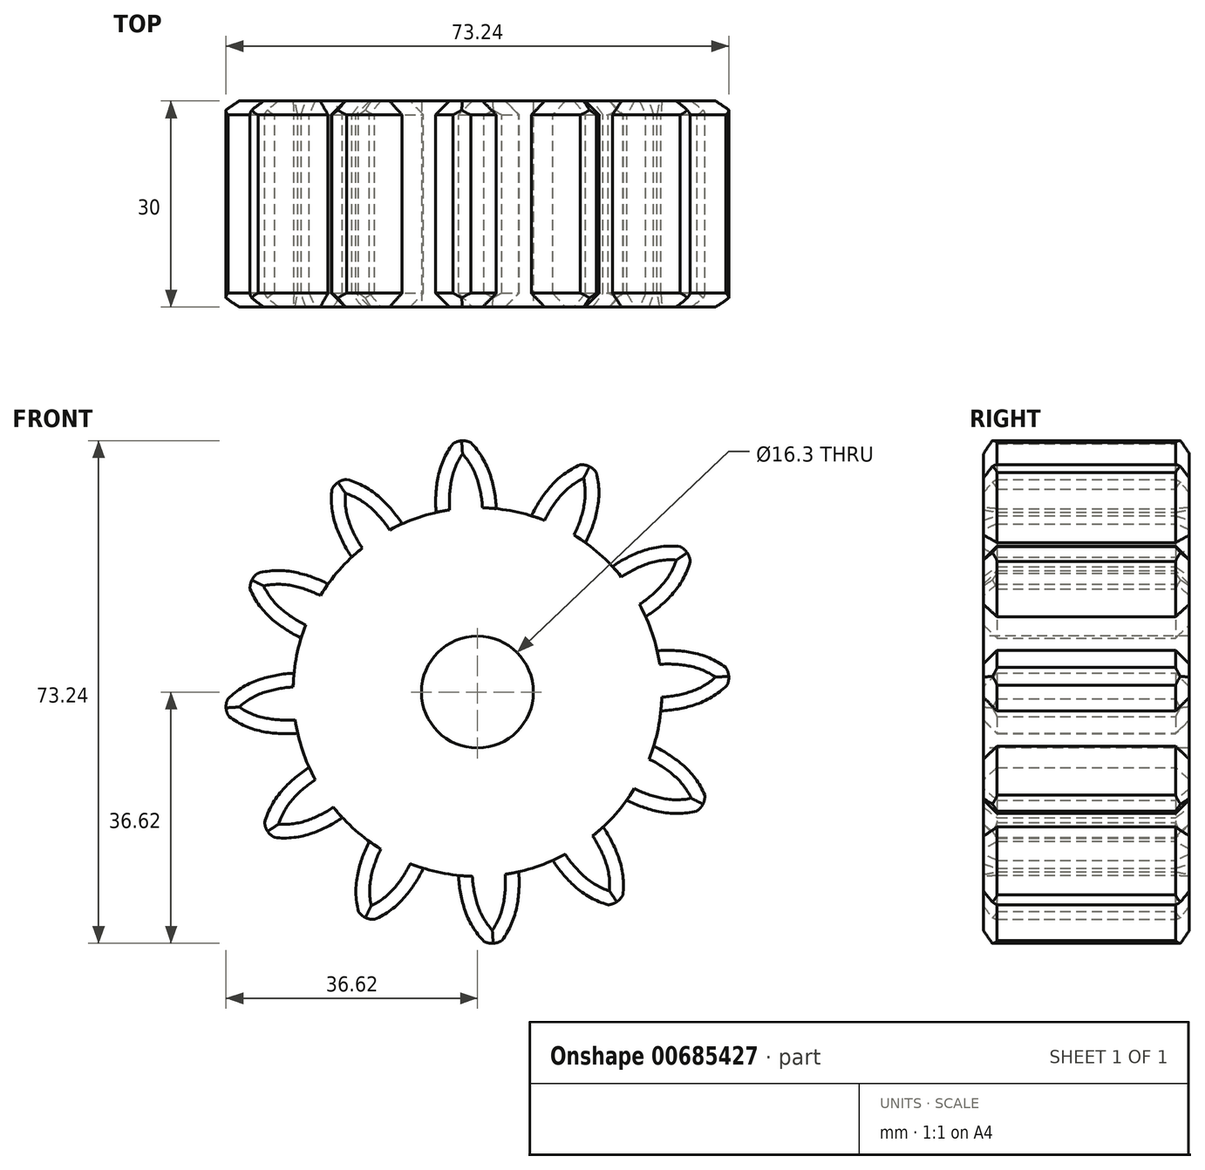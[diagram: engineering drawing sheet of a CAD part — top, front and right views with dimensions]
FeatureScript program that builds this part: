
annotation { "Feature Type Name" : "Feature", "Feature Type Description" : "" }
export const myFeature = defineFeature(function(context is Context, id is Id, definition is map)
    precondition{}
    {
        {
            var Q0;
            Q0=qCreatedBy(makeId("Front.planeOp"),FACE);
            var sketch = newSketch(context, id + "F0", { "sketchPlane" : qUnion([Q0])});
            skCircle(sketch, "E0", {"center": v(0, 0) * mm, "radius": 26.86 * mm});
            skCircle(sketch, "E1", {"center": v(0, 0) * mm, "radius": 29.34 * mm, "construction": true});
            skCircle(sketch, "E2", {"center": v(0, 0) * mm, "radius": 31.75 * mm, "construction": true});
            skLineSegment(sketch, "E3", {"start": v(0, 0) * mm, "end": v(0, 95.44) * mm, "construction": true});
            skLineSegment(sketch, "E4", {"start": v(0, 0) * mm, "end": v(-6.27, 95.6) * mm, "construction": true});
            skLineSegment(sketch, "E5", {"start": v(0, 29.34) * mm, "end": v(-75.4, 29.34) * mm, "construction": true});
            skLineSegment(sketch, "E6", {"start": v(0, 29.34) * mm, "end": v(-75.03, 2.03) * mm, "construction": true});
            skCircle(sketch, "E7", {"center": v(0, 0) * mm, "radius": 27.57 * mm, "construction": true});
            skCircle(sketch, "E8", {"center": v(0, 29.34) * mm, "radius": 14.6 * mm, "construction": true});
            skCircle(sketch, "E9", {"center": v(-13.72, 24.34) * mm, "radius": 14.6 * mm, "construction": true});
            skCircle(sketch, "E10", {"center": v(0, 0) * mm, "radius": 30.86 * mm});
            skArc(sketch, "E11", {"start": v(1.88, 31.6) * mm, "mid": v(0.73, 34.14) * mm, "end": v(-0.98, 36.36) * mm});
            skArc(sketch, "E12", {"start": v(2.76, 26.63) * mm, "mid": v(2.48, 29.14) * mm, "end": v(1.88, 31.6) * mm});
            skArc(sketch, "E13.MirrorCS", {"start": v(-5.78, 31.1) * mm, "mid": v(-4.97, 33.77) * mm, "end": v(-3.57, 36.19) * mm});
            skArc(sketch, "E14.MirrorCS", {"start": v(-6, 26.06) * mm, "mid": v(-6.06, 28.58) * mm, "end": v(-5.78, 31.1) * mm});
            skArc(sketch, "E15", {"start": v(-0.98, 36.36) * mm, "mid": v(-2.3, 36.62) * mm, "end": v(-3.57, 36.19) * mm});
            skSolve(sketch);
        }
        {
            var Q0;
            {var subQ0=sQuery(id+"F0.wireOp",EDGE,"E0");var subQ1=makeQuery(id+"F0.imprint","INTERSECT",VERTEX,{"derivedFrom":[subQ0,sQuery(id+"F0.wireOp",EDGE,"E12")]});Q0=makeQuery(id+"F0.imprint","IMPRINT",FACE,{"disambiguationData":[TD([[makeQuery(id+"F0.imprint","IMPRINT",EDGE,{"disambiguationData":[TD([[subQ1,-1.0]])],"derivedFrom":subQ0}),1.0]])]});}
            var Q1;
            {var subQ1=sQuery(id+"F0.wireOp",EDGE,"E11");Q1=makeQuery(id+"F0.imprint","IMPRINT",FACE,{"disambiguationData":[TD([[makeQuery(id+"F0.imprint","IMPRINT",EDGE,{"derivedFrom":subQ1}),1.0]])]});}
            var Q2;
            {var subQ0=sQuery(id+"F0.wireOp",EDGE,"E12");var subQ1=sQuery(id+"F0.wireOp",EDGE,"E0");var subQ2=makeQuery(id+"F0.imprint","INTERSECT",VERTEX,{"derivedFrom":[subQ1,subQ0]});Q2=makeQuery(id+"F0.imprint","IMPRINT",FACE,{"disambiguationData":[TD([[makeQuery(id+"F0.imprint","IMPRINT",EDGE,{"disambiguationData":[TD([[subQ2,-1.0]])],"derivedFrom":subQ1}),-1.0]])]});}
            extrude(context, id + "F1", {"entities" : qUnion([Q0, Q1, Q2]), "depth" : 30 * mm, "offsetDistance" : 25 * mm});
        }
        {
            var Q0;
            Q0=makeQuery(id+"F1.opExtrude","CAP_EDGE",EDGE,{"disambiguationData":[OSD([sQuery(id+"F0.wireOp",EDGE,"E14.MirrorCS")])],"isStart":false});
            var Q1;
            Q1=makeQuery(id+"F1.opExtrude","CAP_EDGE",EDGE,{"disambiguationData":[OSD([sQuery(id+"F0.wireOp",EDGE,"E12")])],"isStart":false});
            var Q2;
            Q2=makeQuery(id+"F1.opExtrude","CAP_EDGE",EDGE,{"disambiguationData":[OSD([sQuery(id+"F0.wireOp",EDGE,"E14.MirrorCS")])],"isStart":true});
            var Q3;
            Q3=makeQuery(id+"F1.opExtrude","CAP_EDGE",EDGE,{"disambiguationData":[OSD([sQuery(id+"F0.wireOp",EDGE,"E12")])],"isStart":true});
            var Q4;
            Q4=makeQuery(id+"F18UF4900IuEQJn_1.opPattern","COPY",EDGE,{"derivedFrom":makeQuery(id+"F1.opExtrude","CAP_EDGE",EDGE,{"disambiguationData":[OSD([sQuery(id+"F0.wireOp",EDGE,"E14.MirrorCS")])],"isStart":false}),"instanceName":"11"});
            var Q5;
            Q5=makeQuery(id+"F18UF4900IuEQJn_1.opPattern","COPY",EDGE,{"derivedFrom":makeQuery(id+"F1.opExtrude","CAP_EDGE",EDGE,{"disambiguationData":[OSD([sQuery(id+"F0.wireOp",EDGE,"E12")])],"isStart":false}),"instanceName":"11"});
            var Q6;
            Q6=makeQuery(id+"F18UF4900IuEQJn_1.opPattern","COPY",EDGE,{"derivedFrom":makeQuery(id+"F1.opExtrude","CAP_EDGE",EDGE,{"disambiguationData":[OSD([sQuery(id+"F0.wireOp",EDGE,"E14.MirrorCS")])],"isStart":true}),"instanceName":"11"});
            var Q7;
            Q7=makeQuery(id+"F18UF4900IuEQJn_1.opPattern","COPY",EDGE,{"derivedFrom":makeQuery(id+"F1.opExtrude","CAP_EDGE",EDGE,{"disambiguationData":[OSD([sQuery(id+"F0.wireOp",EDGE,"E12")])],"isStart":true}),"instanceName":"11"});
            var Q8;
            Q8=makeQuery(id+"F18UF4900IuEQJn_1.opPattern","COPY",EDGE,{"derivedFrom":makeQuery(id+"F1.opExtrude","CAP_EDGE",EDGE,{"disambiguationData":[OSD([sQuery(id+"F0.wireOp",EDGE,"E14.MirrorCS")])],"isStart":false}),"instanceName":"10"});
            var Q9;
            Q9=makeQuery(id+"F18UF4900IuEQJn_1.opPattern","COPY",EDGE,{"derivedFrom":makeQuery(id+"F1.opExtrude","CAP_EDGE",EDGE,{"disambiguationData":[OSD([sQuery(id+"F0.wireOp",EDGE,"E12")])],"isStart":false}),"instanceName":"10"});
            var Q10;
            Q10=makeQuery(id+"F18UF4900IuEQJn_1.opPattern","COPY",EDGE,{"derivedFrom":makeQuery(id+"F1.opExtrude","CAP_EDGE",EDGE,{"disambiguationData":[OSD([sQuery(id+"F0.wireOp",EDGE,"E14.MirrorCS")])],"isStart":false}),"instanceName":"9"});
            var Q11;
            Q11=makeQuery(id+"F18UF4900IuEQJn_1.opPattern","COPY",EDGE,{"derivedFrom":makeQuery(id+"F1.opExtrude","CAP_EDGE",EDGE,{"disambiguationData":[OSD([sQuery(id+"F0.wireOp",EDGE,"E12")])],"isStart":false}),"instanceName":"9"});
            var Q12;
            Q12=makeQuery(id+"F18UF4900IuEQJn_1.opPattern","COPY",EDGE,{"derivedFrom":makeQuery(id+"F1.opExtrude","CAP_EDGE",EDGE,{"disambiguationData":[OSD([sQuery(id+"F0.wireOp",EDGE,"E14.MirrorCS")])],"isStart":false}),"instanceName":"8"});
            var Q13;
            Q13=makeQuery(id+"F18UF4900IuEQJn_1.opPattern","COPY",EDGE,{"derivedFrom":makeQuery(id+"F1.opExtrude","CAP_EDGE",EDGE,{"disambiguationData":[OSD([sQuery(id+"F0.wireOp",EDGE,"E12")])],"isStart":false}),"instanceName":"8"});
            var Q14;
            Q14=makeQuery(id+"F18UF4900IuEQJn_1.opPattern","COPY",EDGE,{"derivedFrom":makeQuery(id+"F1.opExtrude","CAP_EDGE",EDGE,{"disambiguationData":[OSD([sQuery(id+"F0.wireOp",EDGE,"E14.MirrorCS")])],"isStart":false}),"instanceName":"7"});
            var Q15;
            Q15=makeQuery(id+"F18UF4900IuEQJn_1.opPattern","COPY",EDGE,{"derivedFrom":makeQuery(id+"F1.opExtrude","CAP_EDGE",EDGE,{"disambiguationData":[OSD([sQuery(id+"F0.wireOp",EDGE,"E12")])],"isStart":false}),"instanceName":"7"});
            var Q16;
            Q16=makeQuery(id+"F18UF4900IuEQJn_1.opPattern","COPY",EDGE,{"derivedFrom":makeQuery(id+"F1.opExtrude","CAP_EDGE",EDGE,{"disambiguationData":[OSD([sQuery(id+"F0.wireOp",EDGE,"E12")])],"isStart":false}),"instanceName":"6"});
            var Q17;
            Q17=makeQuery(id+"F18UF4900IuEQJn_1.opPattern","COPY",EDGE,{"derivedFrom":makeQuery(id+"F1.opExtrude","CAP_EDGE",EDGE,{"disambiguationData":[OSD([sQuery(id+"F0.wireOp",EDGE,"E14.MirrorCS")])],"isStart":false}),"instanceName":"6"});
            var Q18;
            Q18=makeQuery(id+"F18UF4900IuEQJn_1.opPattern","COPY",EDGE,{"derivedFrom":makeQuery(id+"F1.opExtrude","CAP_EDGE",EDGE,{"disambiguationData":[OSD([sQuery(id+"F0.wireOp",EDGE,"E12")])],"isStart":false}),"instanceName":"5"});
            var Q19;
            Q19=makeQuery(id+"F18UF4900IuEQJn_1.opPattern","COPY",EDGE,{"derivedFrom":makeQuery(id+"F1.opExtrude","CAP_EDGE",EDGE,{"disambiguationData":[OSD([sQuery(id+"F0.wireOp",EDGE,"E14.MirrorCS")])],"isStart":false}),"instanceName":"5"});
            var Q20;
            Q20=makeQuery(id+"F18UF4900IuEQJn_1.opPattern","COPY",EDGE,{"derivedFrom":makeQuery(id+"F1.opExtrude","CAP_EDGE",EDGE,{"disambiguationData":[OSD([sQuery(id+"F0.wireOp",EDGE,"E12")])],"isStart":false}),"instanceName":"4"});
            var Q21;
            Q21=makeQuery(id+"F18UF4900IuEQJn_1.opPattern","COPY",EDGE,{"derivedFrom":makeQuery(id+"F1.opExtrude","CAP_EDGE",EDGE,{"disambiguationData":[OSD([sQuery(id+"F0.wireOp",EDGE,"E14.MirrorCS")])],"isStart":false}),"instanceName":"4"});
            var Q22;
            Q22=makeQuery(id+"F18UF4900IuEQJn_1.opPattern","COPY",EDGE,{"derivedFrom":makeQuery(id+"F1.opExtrude","CAP_EDGE",EDGE,{"disambiguationData":[OSD([sQuery(id+"F0.wireOp",EDGE,"E12")])],"isStart":false}),"instanceName":"3"});
            var Q23;
            Q23=makeQuery(id+"F18UF4900IuEQJn_1.opPattern","COPY",EDGE,{"derivedFrom":makeQuery(id+"F1.opExtrude","CAP_EDGE",EDGE,{"disambiguationData":[OSD([sQuery(id+"F0.wireOp",EDGE,"E14.MirrorCS")])],"isStart":false}),"instanceName":"3"});
            var Q24;
            Q24=makeQuery(id+"F18UF4900IuEQJn_1.opPattern","COPY",EDGE,{"derivedFrom":makeQuery(id+"F1.opExtrude","CAP_EDGE",EDGE,{"disambiguationData":[OSD([sQuery(id+"F0.wireOp",EDGE,"E12")])],"isStart":false}),"instanceName":"2"});
            var Q25;
            Q25=makeQuery(id+"F18UF4900IuEQJn_1.opPattern","COPY",EDGE,{"derivedFrom":makeQuery(id+"F1.opExtrude","CAP_EDGE",EDGE,{"disambiguationData":[OSD([sQuery(id+"F0.wireOp",EDGE,"E14.MirrorCS")])],"isStart":false}),"instanceName":"2"});
            var Q26;
            Q26=makeQuery(id+"F18UF4900IuEQJn_1.opPattern","COPY",EDGE,{"derivedFrom":makeQuery(id+"F1.opExtrude","CAP_EDGE",EDGE,{"disambiguationData":[OSD([sQuery(id+"F0.wireOp",EDGE,"E12")])],"isStart":false}),"instanceName":"1"});
            var Q27;
            Q27=makeQuery(id+"F18UF4900IuEQJn_1.opPattern","COPY",EDGE,{"derivedFrom":makeQuery(id+"F1.opExtrude","CAP_EDGE",EDGE,{"disambiguationData":[OSD([sQuery(id+"F0.wireOp",EDGE,"E14.MirrorCS")])],"isStart":false}),"instanceName":"1"});
            var Q28;
            Q28=makeQuery(id+"F18UF4900IuEQJn_1.opPattern","COPY",EDGE,{"derivedFrom":makeQuery(id+"F1.opExtrude","CAP_EDGE",EDGE,{"disambiguationData":[OSD([sQuery(id+"F0.wireOp",EDGE,"E12")])],"isStart":true}),"instanceName":"1"});
            var Q29;
            Q29=makeQuery(id+"F18UF4900IuEQJn_1.opPattern","COPY",EDGE,{"derivedFrom":makeQuery(id+"F1.opExtrude","CAP_EDGE",EDGE,{"disambiguationData":[OSD([sQuery(id+"F0.wireOp",EDGE,"E14.MirrorCS")])],"isStart":true}),"instanceName":"1"});
            var Q30;
            Q30=makeQuery(id+"F18UF4900IuEQJn_1.opPattern","COPY",EDGE,{"derivedFrom":makeQuery(id+"F1.opExtrude","CAP_EDGE",EDGE,{"disambiguationData":[OSD([sQuery(id+"F0.wireOp",EDGE,"E14.MirrorCS")])],"isStart":true}),"instanceName":"2"});
            var Q31;
            Q31=makeQuery(id+"F18UF4900IuEQJn_1.opPattern","COPY",EDGE,{"derivedFrom":makeQuery(id+"F1.opExtrude","CAP_EDGE",EDGE,{"disambiguationData":[OSD([sQuery(id+"F0.wireOp",EDGE,"E12")])],"isStart":true}),"instanceName":"2"});
            var Q32;
            Q32=makeQuery(id+"F18UF4900IuEQJn_1.opPattern","COPY",EDGE,{"derivedFrom":makeQuery(id+"F1.opExtrude","CAP_EDGE",EDGE,{"disambiguationData":[OSD([sQuery(id+"F0.wireOp",EDGE,"E14.MirrorCS")])],"isStart":true}),"instanceName":"3"});
            var Q33;
            Q33=makeQuery(id+"F18UF4900IuEQJn_1.opPattern","COPY",EDGE,{"derivedFrom":makeQuery(id+"F1.opExtrude","CAP_EDGE",EDGE,{"disambiguationData":[OSD([sQuery(id+"F0.wireOp",EDGE,"E12")])],"isStart":true}),"instanceName":"3"});
            var Q34;
            Q34=makeQuery(id+"F18UF4900IuEQJn_1.opPattern","COPY",EDGE,{"derivedFrom":makeQuery(id+"F1.opExtrude","CAP_EDGE",EDGE,{"disambiguationData":[OSD([sQuery(id+"F0.wireOp",EDGE,"E14.MirrorCS")])],"isStart":true}),"instanceName":"4"});
            var Q35;
            Q35=makeQuery(id+"F18UF4900IuEQJn_1.opPattern","COPY",EDGE,{"derivedFrom":makeQuery(id+"F1.opExtrude","CAP_EDGE",EDGE,{"disambiguationData":[OSD([sQuery(id+"F0.wireOp",EDGE,"E12")])],"isStart":true}),"instanceName":"4"});
            var Q36;
            Q36=makeQuery(id+"F18UF4900IuEQJn_1.opPattern","COPY",EDGE,{"derivedFrom":makeQuery(id+"F1.opExtrude","CAP_EDGE",EDGE,{"disambiguationData":[OSD([sQuery(id+"F0.wireOp",EDGE,"E14.MirrorCS")])],"isStart":true}),"instanceName":"5"});
            var Q37;
            Q37=makeQuery(id+"F18UF4900IuEQJn_1.opPattern","COPY",EDGE,{"derivedFrom":makeQuery(id+"F1.opExtrude","CAP_EDGE",EDGE,{"disambiguationData":[OSD([sQuery(id+"F0.wireOp",EDGE,"E12")])],"isStart":true}),"instanceName":"5"});
            var Q38;
            Q38=makeQuery(id+"F18UF4900IuEQJn_1.opPattern","COPY",EDGE,{"derivedFrom":makeQuery(id+"F1.opExtrude","CAP_EDGE",EDGE,{"disambiguationData":[OSD([sQuery(id+"F0.wireOp",EDGE,"E14.MirrorCS")])],"isStart":true}),"instanceName":"6"});
            var Q39;
            Q39=makeQuery(id+"F18UF4900IuEQJn_1.opPattern","COPY",EDGE,{"derivedFrom":makeQuery(id+"F1.opExtrude","CAP_EDGE",EDGE,{"disambiguationData":[OSD([sQuery(id+"F0.wireOp",EDGE,"E12")])],"isStart":true}),"instanceName":"6"});
            var Q40;
            Q40=makeQuery(id+"F18UF4900IuEQJn_1.opPattern","COPY",EDGE,{"derivedFrom":makeQuery(id+"F1.opExtrude","CAP_EDGE",EDGE,{"disambiguationData":[OSD([sQuery(id+"F0.wireOp",EDGE,"E14.MirrorCS")])],"isStart":true}),"instanceName":"7"});
            var Q41;
            Q41=makeQuery(id+"F18UF4900IuEQJn_1.opPattern","COPY",EDGE,{"derivedFrom":makeQuery(id+"F1.opExtrude","CAP_EDGE",EDGE,{"disambiguationData":[OSD([sQuery(id+"F0.wireOp",EDGE,"E12")])],"isStart":true}),"instanceName":"7"});
            var Q42;
            Q42=makeQuery(id+"F18UF4900IuEQJn_1.opPattern","COPY",EDGE,{"derivedFrom":makeQuery(id+"F1.opExtrude","CAP_EDGE",EDGE,{"disambiguationData":[OSD([sQuery(id+"F0.wireOp",EDGE,"E14.MirrorCS")])],"isStart":true}),"instanceName":"8"});
            var Q43;
            Q43=makeQuery(id+"F18UF4900IuEQJn_1.opPattern","COPY",EDGE,{"derivedFrom":makeQuery(id+"F1.opExtrude","CAP_EDGE",EDGE,{"disambiguationData":[OSD([sQuery(id+"F0.wireOp",EDGE,"E12")])],"isStart":true}),"instanceName":"8"});
            var Q44;
            Q44=makeQuery(id+"F18UF4900IuEQJn_1.opPattern","COPY",EDGE,{"derivedFrom":makeQuery(id+"F1.opExtrude","CAP_EDGE",EDGE,{"disambiguationData":[OSD([sQuery(id+"F0.wireOp",EDGE,"E14.MirrorCS")])],"isStart":true}),"instanceName":"9"});
            var Q45;
            Q45=makeQuery(id+"F18UF4900IuEQJn_1.opPattern","COPY",EDGE,{"derivedFrom":makeQuery(id+"F1.opExtrude","CAP_EDGE",EDGE,{"disambiguationData":[OSD([sQuery(id+"F0.wireOp",EDGE,"E12")])],"isStart":true}),"instanceName":"9"});
            var Q46;
            Q46=makeQuery(id+"F18UF4900IuEQJn_1.opPattern","COPY",EDGE,{"derivedFrom":makeQuery(id+"F1.opExtrude","CAP_EDGE",EDGE,{"disambiguationData":[OSD([sQuery(id+"F0.wireOp",EDGE,"E14.MirrorCS")])],"isStart":true}),"instanceName":"10"});
            var Q47;
            Q47=makeQuery(id+"F18UF4900IuEQJn_1.opPattern","COPY",EDGE,{"derivedFrom":makeQuery(id+"F1.opExtrude","CAP_EDGE",EDGE,{"disambiguationData":[OSD([sQuery(id+"F0.wireOp",EDGE,"E12")])],"isStart":true}),"instanceName":"10"});
            chamfer(context, id + "F2", {"entities" : qUnion([Q0, Q1, Q2, Q3, Q4, Q5, Q6, Q7, Q8, Q9, Q10, Q11, Q12, Q13, Q14, Q15, Q16, Q17, Q18, Q19, Q20, Q21, Q22, Q23, Q24, Q25, Q26, Q27, Q28, Q29, Q30, Q31, Q32, Q33, Q34, Q35, Q36, Q37, Q38, Q39, Q40, Q41, Q42, Q43, Q44, Q45, Q46, Q47]), "width" : 2 * mm, "tangentPropagation" : true});
        }
        {
            var Q0;
            Q0=makeQuery(id+"F1.opExtrude","CAP_FACE",FACE,{"disambiguationData":[OSD([sQuery(id+"F0.wireOp",EDGE,"E0"),sQuery(id+"F0.wireOp",EDGE,"E11"),sQuery(id+"F0.wireOp",EDGE,"E12"),sQuery(id+"F0.wireOp",EDGE,"E13.MirrorCS"),sQuery(id+"F0.wireOp",EDGE,"E14.MirrorCS"),sQuery(id+"F0.wireOp",EDGE,"E15")])],"isStart":false});
            var sketch = newSketch(context, id + "F3", { "sketchPlane" : qUnion([Q0])});
            skPoint(sketch, "E16.0.midPoint", {"position": v(5.03, -3.02) * mm});
            skCircle(sketch, "E17", {"center": v(0, 0) * mm, "radius": 8.15 * mm});
            skSolve(sketch);
        }
        {
            var Q0;
            Q0=makeQuery(id+"F3.imprint","IMPRINT",FACE,{"disambiguationData":[TD([[makeQuery(id+"F3.imprint","IMPRINT",EDGE,{"derivedFrom":sQuery(id+"F3.wireOp",EDGE,"E16.0")}),-1.0]])]});
            var Q1;
            Q1=makeQuery(id+"F3.imprint","IMPRINT",FACE,{"disambiguationData":[TD([[makeQuery(id+"F3.imprint","IMPRINT",EDGE,{"derivedFrom":sQuery(id+"F3.wireOp",EDGE,"E17")}),1.0]])]});
            extrude(context, id + "F4", {"entities" : qUnion([Q0, Q1]), "operationType" : NewBodyOperationType.REMOVE, "oppositeDirection" : true, "depth" : 32 * mm, "offsetDistance" : 25 * mm});
        }
        {
            var Q0;
            Q0=makeQuery(id+"F1.opExtrude","SWEPT_BODY",BODY,{"disambiguationData":[OSD([sQuery(id+"F0.wireOp",EDGE,"E0"),sQuery(id+"F0.wireOp",EDGE,"E11"),sQuery(id+"F0.wireOp",EDGE,"E12"),sQuery(id+"F0.wireOp",EDGE,"E13.MirrorCS"),sQuery(id+"F0.wireOp",EDGE,"E14.MirrorCS"),sQuery(id+"F0.wireOp",EDGE,"E15")])]});
            var Q1;
            Q1=makeQuery(id+"F1.opExtrude","SWEPT_FACE",FACE,{"disambiguationData":[OSD([sQuery(id+"F0.wireOp",EDGE,"E0")])]});
            circularPattern(context, id + "F5", {"operationType" : NewBodyOperationType.ADD, "entities" : qUnion([Q0]), "axis" : qUnion([Q1]), "angle" : 360 * degree, "instanceCount" : 12, "equalSpace" : true});
        }
    });
